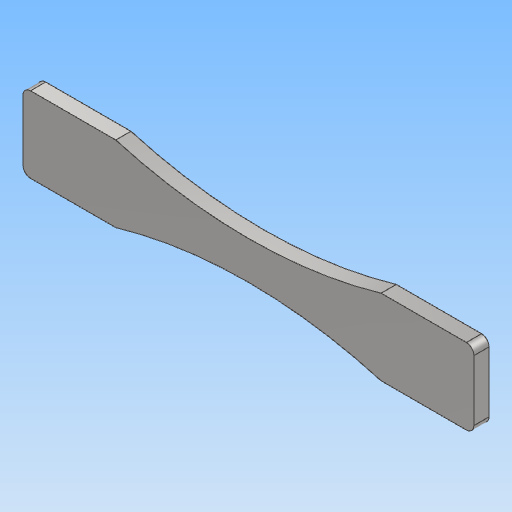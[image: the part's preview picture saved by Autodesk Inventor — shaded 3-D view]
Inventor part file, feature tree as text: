
AUTODESK INVENTOR PART (.ipt)
format: ipt  version: 2020 (Build 240168000, 168)  size: 125,952 bytes
history: native  units: mm
features: other x1, extrude x1
ambient origin geometry x8: Origin, YZ Plane, XZ Plane, XY Plane, X Axis, Y Axis, Z Axis, Center Point
bodies: Body1 (feature_tree)
feature tree (2):
  other  "實體1"
  extrude  "擠出1"  Depth=59.5mm
